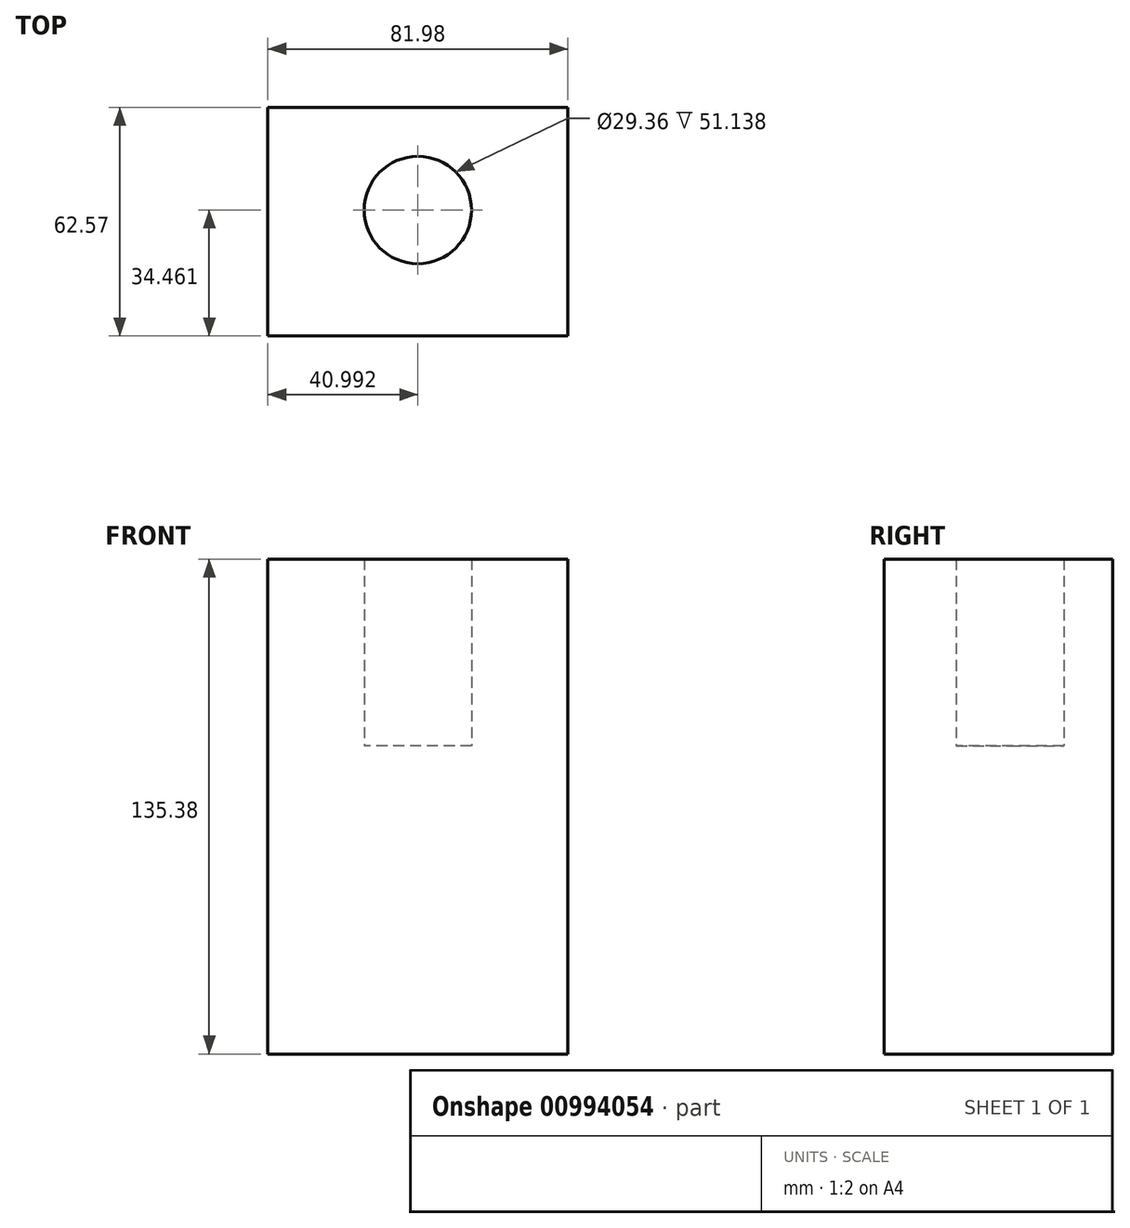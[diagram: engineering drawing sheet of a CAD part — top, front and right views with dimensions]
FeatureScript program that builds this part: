
annotation { "Feature Type Name" : "Feature", "Feature Type Description" : "" }
export const myFeature = defineFeature(function(context is Context, id is Id, definition is map)
    precondition{}
    {
        {
            var Q0;
            Q0=qCreatedBy(makeId("Top.planeOp"),FACE);
            var sketch = newSketch(context, id + "F0", { "sketchPlane" : qUnion([Q0])});
            skLineSegment(sketch, "E0.bottom", {"start": v(81.98, 62.57) * mm, "end": v(0, 62.57) * mm});
            skLineSegment(sketch, "E0.top", {"start": v(81.98, 0) * mm, "end": v(0, 0) * mm});
            skLineSegment(sketch, "E0.left", {"start": v(81.98, 62.57) * mm, "end": v(81.98, 0) * mm});
            skLineSegment(sketch, "E0.right", {"start": v(0, 62.57) * mm, "end": v(0, 0) * mm});
            skLineSegment(sketch, "E1.bottom", {"start": v(13.71, 95.03) * mm, "end": v(15.42, 95.03) * mm});
            skLineSegment(sketch, "E1.top", {"start": v(13.71, 71.55) * mm, "end": v(15.42, 71.55) * mm});
            skLineSegment(sketch, "E1.left", {"start": v(13.71, 95.03) * mm, "end": v(13.71, 71.55) * mm});
            skLineSegment(sketch, "E1.right", {"start": v(15.42, 95.03) * mm, "end": v(15.42, 71.55) * mm});
            skSolve(sketch);
        }
        {
            var Q0;
            Q0=makeQuery(id+"F0.imprint","IMPRINT",FACE,{"disambiguationData":[TD([[makeQuery(id+"F0.imprint","IMPRINT",EDGE,{"derivedFrom":sQuery(id+"F0.wireOp",EDGE,"E0.bottom")}),1.0]])]});
            extrude(context, id + "F1", {"entities" : qUnion([Q0]), "depth" : 84.24 * mm, "offsetDistance" : 25.4 * mm});
        }
        {
            var Q0;
            Q0=makeQuery(id+"F1.opExtrude","CAP_FACE",FACE,{"disambiguationData":[OSD([sQuery(id+"F0.wireOp",EDGE,"E0.bottom"),sQuery(id+"F0.wireOp",EDGE,"E0.top"),sQuery(id+"F0.wireOp",EDGE,"E0.left"),sQuery(id+"F0.wireOp",EDGE,"E0.right")])],"isStart":false});
            var sketch = newSketch(context, id + "F2", { "sketchPlane" : qUnion([Q0])});
            skCircle(sketch, "E2", {"center": v(41, 34.46) * mm, "radius": 14.68 * mm});
            skPoint(sketch, "E2.centerSnap0", {"position": v(41, 62.57) * mm});
            skSolve(sketch);
        }
        {
            var Q0;
            Q0=makeQuery(id+"F2.imprint","IMPRINT",FACE,{"disambiguationData":[TD([[makeQuery(id+"F2.imprint","IMPRINT",EDGE,{"derivedFrom":sQuery(id+"F2.wireOp",EDGE,"E2")}),-1.0]])]});
            extrude(context, id + "F3", {"entities" : qUnion([Q0]), "operationType" : NewBodyOperationType.ADD, "depth" : 51.14 * mm, "offsetDistance" : 25.4 * mm});
        }
    });
